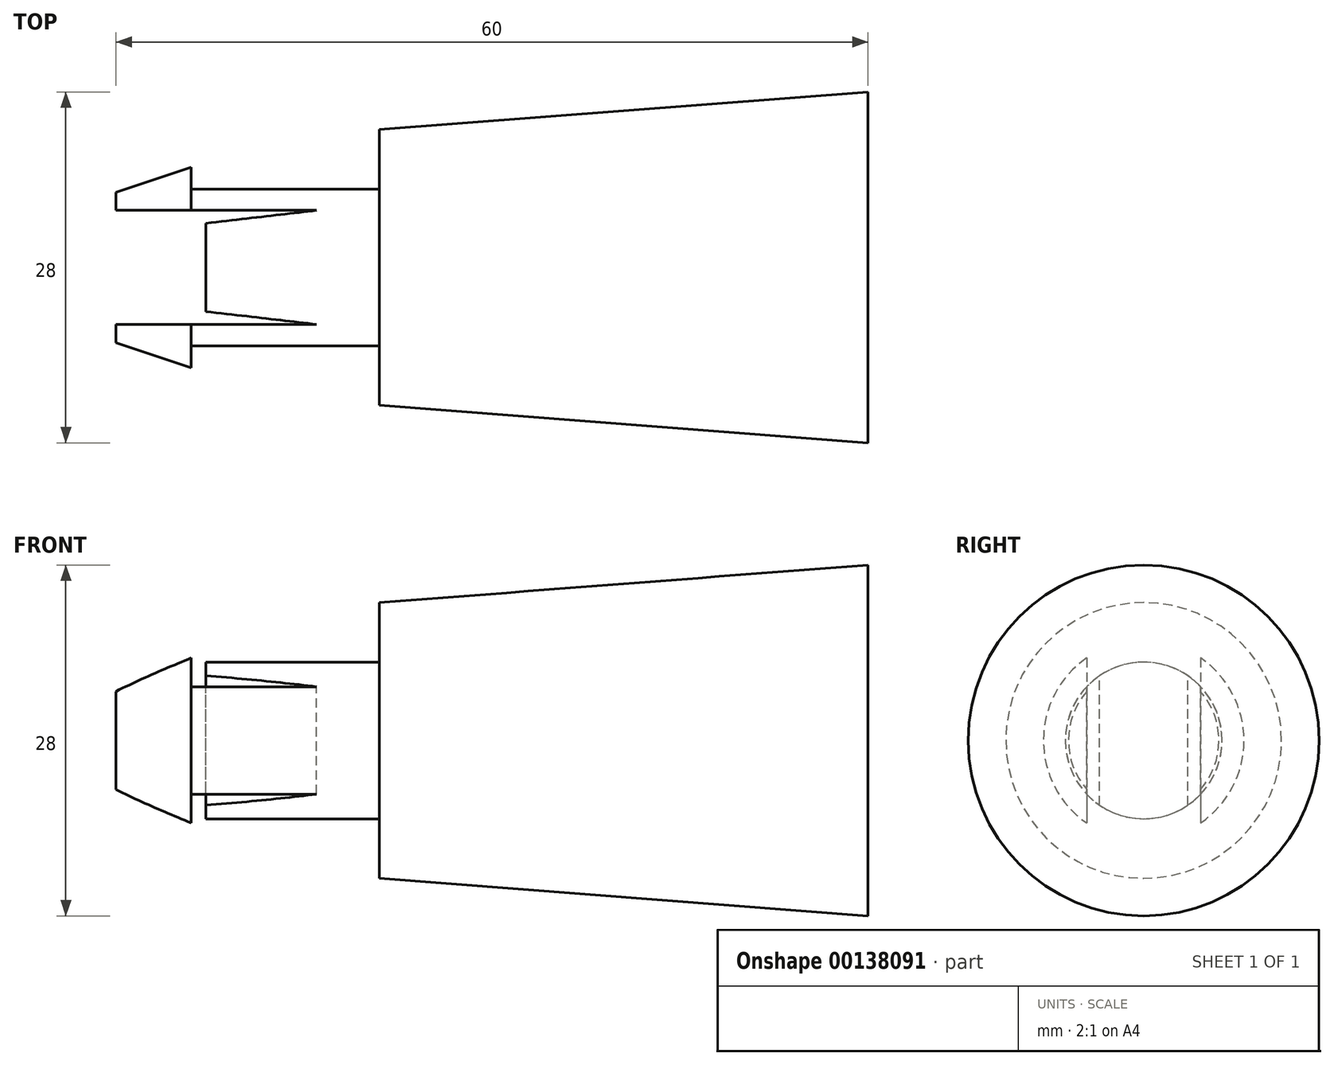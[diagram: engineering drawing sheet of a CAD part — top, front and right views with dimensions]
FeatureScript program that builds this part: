
annotation { "Feature Type Name" : "Feature", "Feature Type Description" : "" }
export const myFeature = defineFeature(function(context is Context, id is Id, definition is map)
    precondition{}
    {
        {
            var Q0;
            Q0=qCreatedBy(makeId("Top.planeOp"),FACE);
            var sketch = newSketch(context, id + "F0", { "sketchPlane" : qUnion([Q0])});
            skLineSegment(sketch, "E0", {"start": v(-141.2, 0) * mm, "end": v(147.54, 0) * mm});
            skSolve(sketch);
        }
        {
            var Q0;
            Q0=qCreatedBy(makeId("Top.planeOp"),FACE);
            var sketch = newSketch(context, id + "F1", { "sketchPlane" : qUnion([Q0])});
            skLineSegment(sketch, "E1", {"start": v(0, 0) * mm, "end": v(39, 0) * mm});
            skLineSegment(sketch, "E2", {"start": v(39, 0) * mm, "end": v(39, 14) * mm});
            skLineSegment(sketch, "E3", {"start": v(39, 14) * mm, "end": v(0, 11) * mm});
            skLineSegment(sketch, "E4", {"start": v(0, 11) * mm, "end": v(0, 0) * mm});
            skSolve(sketch);
        }
        {
            var Q0;
            Q0=makeQuery(id+"F1.imprint","IMPRINT",FACE,{"disambiguationData":[TD([[makeQuery(id+"F1.imprint","IMPRINT",EDGE,{"derivedFrom":sQuery(id+"F1.wireOp",EDGE,"E1")}),1.0]])]});
            var Q1;
            Q1=sQuery(id+"F0.wireOp",EDGE,"E0");
            revolve(context, id + "F2", {"entities" : qUnion([Q0]), "axis" : qUnion([Q1]), "revolveType" : RevolveType.FULL});
        }
        {
            var Q0;
            Q0=qCreatedBy(makeId("Top.planeOp"),FACE);
            var sketch = newSketch(context, id + "F3", { "sketchPlane" : qUnion([Q0])});
            skLineSegment(sketch, "E5", {"start": v(0, 0) * mm, "end": v(-15, 0) * mm});
            skLineSegment(sketch, "E6", {"start": v(-15, 0) * mm, "end": v(-15, 6.25) * mm});
            skLineSegment(sketch, "E7", {"start": v(-15, 6.25) * mm, "end": v(0, 6.25) * mm});
            skLineSegment(sketch, "E8", {"start": v(0, 6.25) * mm, "end": v(0, 1.08) * mm});
            skLineSegment(sketch, "E9", {"start": v(0, 1.08) * mm, "end": v(0, 0) * mm});
            skSolve(sketch);
        }
        {
            var Q0;
            Q0 = qSketchRegion(id + "F3", true);
            var Q1;
            Q1=sQuery(id+"F3.wireOp",EDGE,"E5");
            revolve(context, id + "F4", {"operationType" : NewBodyOperationType.ADD, "entities" : qUnion([Q0]), "axis" : qUnion([Q1]), "revolveType" : RevolveType.FULL});
        }
        {
            var Q0;
            Q0=qCreatedBy(makeId("Top.planeOp"),FACE);
            var sketch = newSketch(context, id + "F5", { "sketchPlane" : qUnion([Q0])});
            skLineSegment(sketch, "E10", {"start": v(-15, 0) * mm, "end": v(-15, 8) * mm});
            skLineSegment(sketch, "E11", {"start": v(-15, 0) * mm, "end": v(-21, 0) * mm});
            skLineSegment(sketch, "E12", {"start": v(-21, 0) * mm, "end": v(-21, 6) * mm});
            skLineSegment(sketch, "E13", {"start": v(-21, 6) * mm, "end": v(-15, 8) * mm});
            skSolve(sketch);
        }
        {
            var Q0;
            Q0 = qSketchRegion(id + "F5", true);
            var Q1;
            Q1=sQuery(id+"F5.wireOp",EDGE,"E11");
            revolve(context, id + "F6", {"operationType" : NewBodyOperationType.ADD, "entities" : qUnion([Q0]), "axis" : qUnion([Q1]), "revolveType" : RevolveType.FULL});
        }
        {
            var Q0;
            Q0=qCreatedBy(makeId("Top.planeOp"),FACE);
            var sketch = newSketch(context, id + "F7", { "sketchPlane" : qUnion([Q0])});
            skLineSegment(sketch, "E14", {"start": v(-23.68, 4.55) * mm, "end": v(-5, 4.55) * mm});
            skLineSegment(sketch, "E15", {"start": v(-5, 4.55) * mm, "end": v(-13.82, 3.52) * mm});
            skLineSegment(sketch, "E16", {"start": v(-13.82, 3.52) * mm, "end": v(-13.82, 0) * mm});
            skLineSegment(sketch, "E17", {"start": v(-13.82, 0) * mm, "end": v(-23.78, 0) * mm});
            skLineSegment(sketch, "E18", {"start": v(-23.78, 0) * mm, "end": v(-23.68, 4.55) * mm});
            skLineSegment(sketch, "E19.MirrorCS", {"start": v(-23.78, 0) * mm, "end": v(-23.68, -4.55) * mm});
            skLineSegment(sketch, "E20.MirrorCS", {"start": v(-23.68, -4.55) * mm, "end": v(-5, -4.55) * mm});
            skLineSegment(sketch, "E21.MirrorCS", {"start": v(-13.82, -3.52) * mm, "end": v(-13.82, 0) * mm});
            skLineSegment(sketch, "E22.MirrorCS", {"start": v(-5, -4.55) * mm, "end": v(-13.82, -3.52) * mm});
            skSolve(sketch);
        }
        {
            var Q0;
            Q0=makeQuery(id+"F7.imprint","IMPRINT",FACE,{"disambiguationData":[TD([[makeQuery(id+"F7.imprint","IMPRINT",EDGE,{"derivedFrom":sQuery(id+"F7.wireOp",EDGE,"E14")}),-1.0]])]});
            var Q1;
            Q1=makeQuery(id+"F7.imprint","IMPRINT",FACE,{"disambiguationData":[TD([[makeQuery(id+"F7.imprint","IMPRINT",EDGE,{"derivedFrom":sQuery(id+"F7.wireOp",EDGE,"E17")}),1.0]])]});
            extrude(context, id + "F8", {"entities" : qUnion([Q0, Q1]), "operationType" : NewBodyOperationType.REMOVE, "endBound" : BoundingType.SYMMETRIC, "oppositeDirection" : true, "depth" : 50 * mm});
        }
    });
